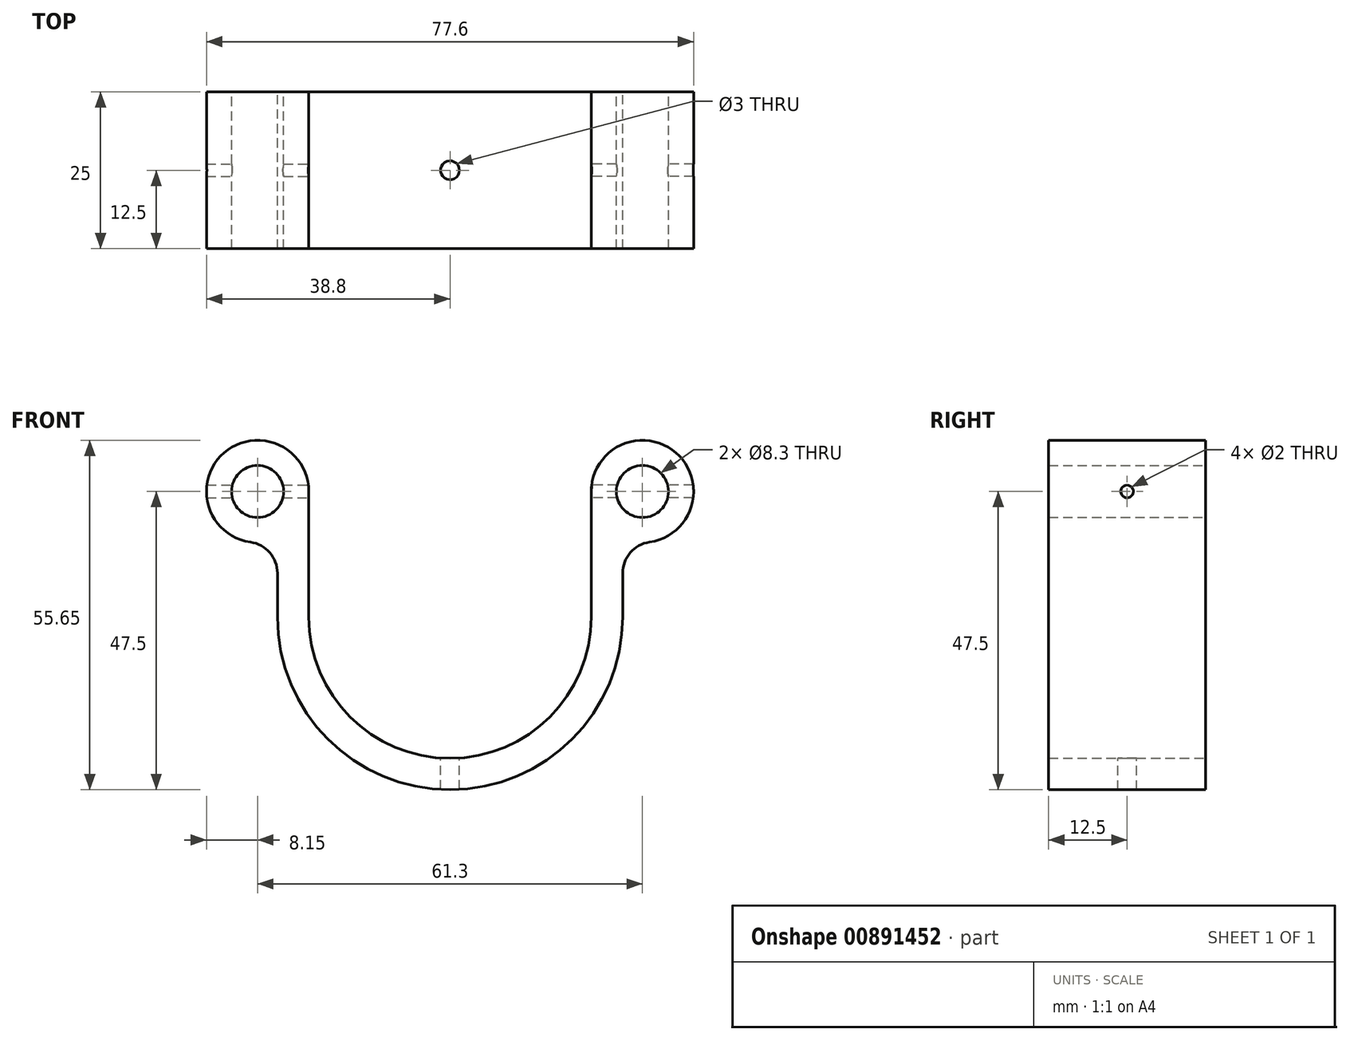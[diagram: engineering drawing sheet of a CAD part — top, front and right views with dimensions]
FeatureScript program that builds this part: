
annotation { "Feature Type Name" : "Feature", "Feature Type Description" : "" }
export const myFeature = defineFeature(function(context is Context, id is Id, definition is map)
    precondition{}
    {
        {
            var Q0;
            Q0=qCreatedBy(makeId("Front.planeOp"),FACE);
            var sketch = newSketch(context, id + "F0", { "sketchPlane" : qUnion([Q0])});
            skLineSegment(sketch, "E0", {"start": v(-22.5, 0) * mm, "end": v(-22.5, -20) * mm});
            skLineSegment(sketch, "E1.MirrorCS", {"start": v(22.5, 0) * mm, "end": v(22.5, -20) * mm});
            skArc(sketch, "E2", {"start": v(-22.5, -20) * mm, "mid": v(0, -42.5) * mm, "end": v(22.5, -20) * mm});
            skCircle(sketch, "E3", {"center": v(-30.65, 0) * mm, "radius": 4.15 * mm});
            skArc(sketch, "E4.0", {"start": v(-27.5, -20) * mm, "mid": v(0, -47.5) * mm, "end": v(27.5, -20) * mm});
            skArc(sketch, "E5", {"start": v(-22.5, 0) * mm, "mid": v(-36, 6.15) * mm, "end": v(-31.8, -8.07) * mm});
            skLineSegment(sketch, "E6", {"start": v(-27.5, -20) * mm, "end": v(-27.5, -13.02) * mm});
            skPoint(sketch, "E7.visualSharp", {"position": v(-27.5, -7.52) * mm});
            skArc(sketch, "E7.filletArc", {"start": v(-27.5, -13.02) * mm, "mid": v(-28.72, -9.74) * mm, "end": v(-31.8, -8.07) * mm});
            skCircle(sketch, "E8.MirrorC", {"center": v(30.65, 0) * mm, "radius": 4.15 * mm});
            skArc(sketch, "E9.MirrorCS", {"start": v(22.5, 0) * mm, "mid": v(36, 6.15) * mm, "end": v(31.8, -8.07) * mm});
            skArc(sketch, "E10.MirrorCS", {"start": v(27.5, -13.02) * mm, "mid": v(28.72, -9.74) * mm, "end": v(31.8, -8.07) * mm});
            skLineSegment(sketch, "E11.MirrorCS", {"start": v(27.5, -20) * mm, "end": v(27.5, -13.02) * mm});
            skSolve(sketch);
        }
        {
            var Q0;
            Q0=makeQuery(id+"F0.imprint","IMPRINT",FACE,{"disambiguationData":[TD([[makeQuery(id+"F0.imprint","IMPRINT",EDGE,{"derivedFrom":sQuery(id+"F0.wireOp",EDGE,"E0")}),-1.0]])]});
            extrude(context, id + "F1", {"entities" : qUnion([Q0]), "depth" : 25 * mm, "offsetDistance" : 25 * mm});
        }
        {
            var Q0;
            Q0=qCreatedBy(makeId("Top.planeOp"),FACE);
            var sketch = newSketch(context, id + "F2", { "sketchPlane" : qUnion([Q0])});
            skCircle(sketch, "E12", {"center": v(0, -12.5) * mm, "radius": 1.5 * mm});
            skSolve(sketch);
        }
        {
            var Q0;
            Q0 = qSketchRegion(id + "F2", true);
            extrude(context, id + "F3", {"entities" : qUnion([Q0]), "operationType" : NewBodyOperationType.REMOVE, "endBound" : BoundingType.THROUGH_ALL, "oppositeDirection" : true, "depth" : 25 * mm, "offsetDistance" : 25 * mm});
        }
        {
            var Q0;
            Q0=qCreatedBy(makeId("Right.planeOp"),FACE);
            var sketch = newSketch(context, id + "F4", { "sketchPlane" : qUnion([Q0])});
            skCircle(sketch, "E13", {"center": v(-12.5, 0) * mm, "radius": 1 * mm});
            skSolve(sketch);
        }
        {
            var Q0;
            Q0 = qSketchRegion(id + "F4", true);
            extrude(context, id + "F5", {"entities" : qUnion([Q0]), "operationType" : NewBodyOperationType.REMOVE, "endBound" : BoundingType.THROUGH_ALL, "depth" : 60 * mm, "offsetDistance" : 25 * mm});
        }
        {
            var Q0;
            Q0 = qSketchRegion(id + "F4", true);
            extrude(context, id + "F6", {"entities" : qUnion([Q0]), "operationType" : NewBodyOperationType.REMOVE, "endBound" : BoundingType.THROUGH_ALL, "oppositeDirection" : true, "depth" : 25 * mm, "offsetDistance" : 25 * mm});
        }
    });
